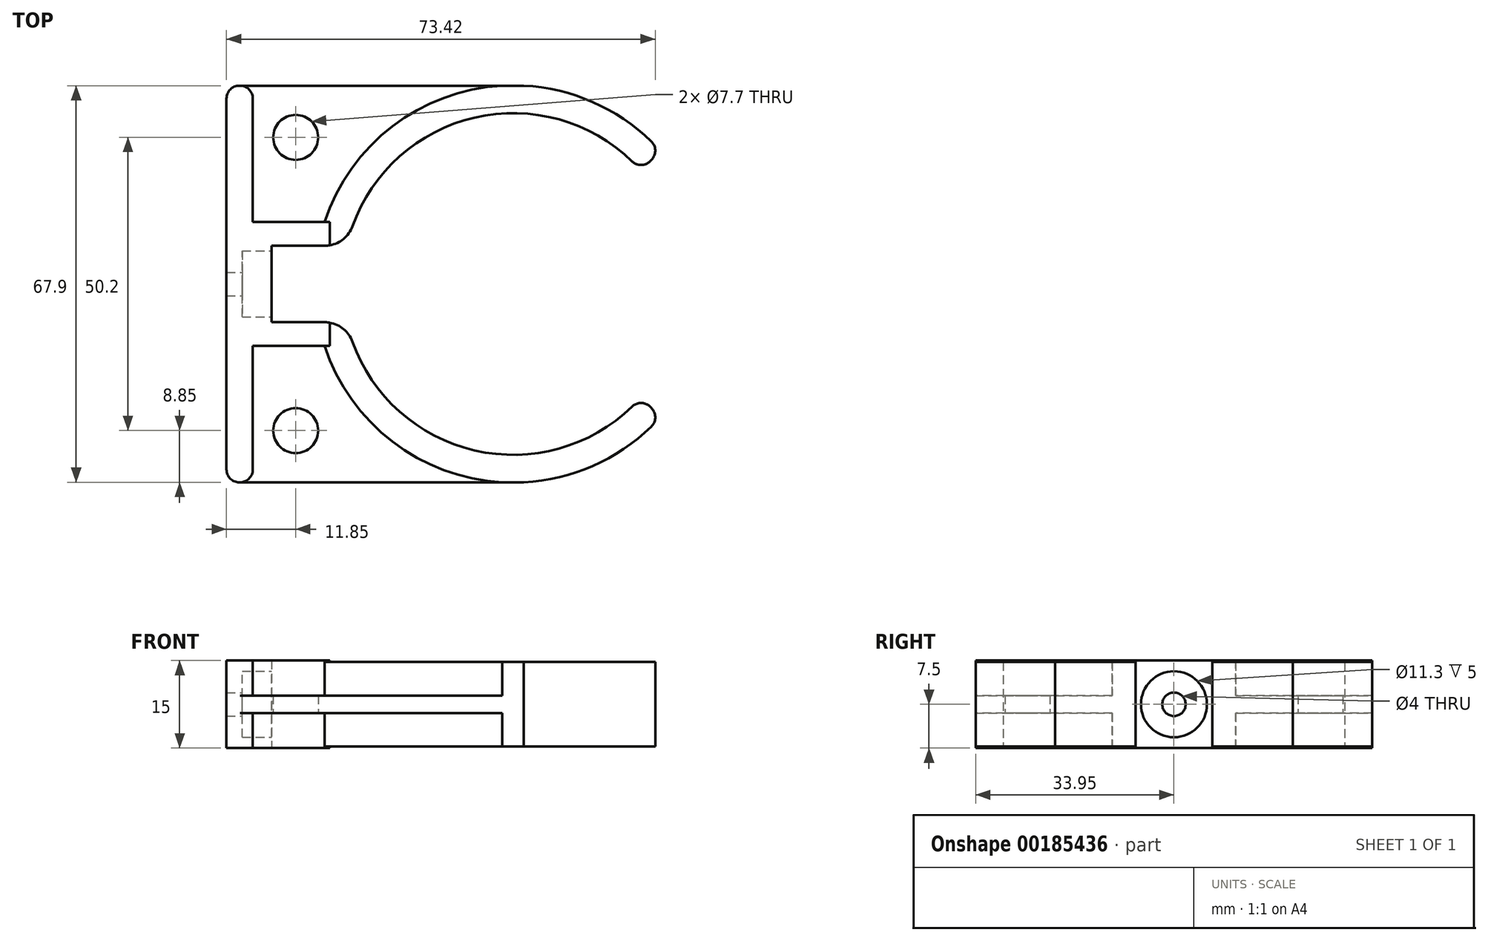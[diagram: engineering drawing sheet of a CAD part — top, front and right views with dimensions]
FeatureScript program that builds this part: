
annotation { "Feature Type Name" : "Feature", "Feature Type Description" : "" }
export const myFeature = defineFeature(function(context is Context, id is Id, definition is map)
    precondition{}
    {
        {
            var Q0;
            Q0=qCreatedBy(makeId("Top.planeOp"),FACE);
            var sketch = newSketch(context, id + "F0", { "sketchPlane" : qUnion([Q0])});
            skLineSegment(sketch, "E0.bottom", {"start": v(0.06, 33.95) * mm, "end": v(-0.06, 33.95) * mm});
            skLineSegment(sketch, "E0.top", {"start": v(0.06, -33.95) * mm, "end": v(-0.06, -33.95) * mm});
            skLineSegment(sketch, "E0.left", {"start": v(2.25, 31.76) * mm, "end": v(2.25, -31.76) * mm});
            skLineSegment(sketch, "E0.right", {"start": v(-2.25, 31.76) * mm, "end": v(-2.25, -31.76) * mm});
            skPoint(sketch, "E0.middle", {"position": v(0, 0) * mm});
            skPoint(sketch, "E1.visualSharp", {"position": v(-2.25, 33.95) * mm});
            skArc(sketch, "E1.filletArc", {"start": v(-0.06, 33.95) * mm, "mid": v(-1.6, 33.3) * mm, "end": v(-2.25, 31.76) * mm});
            skPoint(sketch, "E2.visualSharp", {"position": v(2.25, 33.95) * mm});
            skArc(sketch, "E2.filletArc", {"start": v(2.25, 31.76) * mm, "mid": v(1.6, 33.3) * mm, "end": v(0.06, 33.95) * mm});
            skPoint(sketch, "E3.visualSharp", {"position": v(-2.25, -33.95) * mm});
            skArc(sketch, "E3.filletArc", {"start": v(-2.25, -31.76) * mm, "mid": v(-1.6, -33.3) * mm, "end": v(-0.06, -33.95) * mm});
            skPoint(sketch, "E4.visualSharp", {"position": v(2.25, -33.95) * mm});
            skArc(sketch, "E4.filletArc", {"start": v(0.06, -33.95) * mm, "mid": v(1.6, -33.3) * mm, "end": v(2.25, -31.76) * mm});
            skSolve(sketch);
        }
        {
            var Q0;
            Q0 = qSketchRegion(id + "F0", true);
            extrude(context, id + "F1", {"entities" : qUnion([Q0]), "endBound" : BoundingType.SYMMETRIC, "depth" : 15 * mm});
        }
        {
            var Q0;
            Q0=qCreatedBy(makeId("Right.planeOp"),FACE);
            var sketch = newSketch(context, id + "F2", { "sketchPlane" : qUnion([Q0])});
            skLineSegment(sketch, "E5.left", {"start": v(10.6, 7.5) * mm, "end": v(10.6, -7.5) * mm});
            skLineSegment(sketch, "E5.right", {"start": v(-10.6, 7.5) * mm, "end": v(-10.6, -7.5) * mm});
            skPoint(sketch, "E5.middle", {"position": v(0, 0) * mm});
            skLineSegment(sketch, "E6.0.0", {"start": v(-10.6, -7.5) * mm, "end": v(10.6, -7.5) * mm});
            skLineSegment(sketch, "E6.0.2", {"start": v(10.6, 7.5) * mm, "end": v(-10.6, 7.5) * mm});
            skPoint(sketch, "E7.orphan", {"position": v(-10.6, 13.01) * mm});
            skPoint(sketch, "E8.orphan", {"position": v(10.6, 13.01) * mm});
            skPoint(sketch, "E5.top.start.orphan", {"position": v(10.6, -13.01) * mm});
            skPoint(sketch, "E9.orphan", {"position": v(-10.6, -13.01) * mm});
            skLineSegment(sketch, "E10", {"start": v(0, 7.5) * mm, "end": v(0, -7.5) * mm, "construction": true});
            skPoint(sketch, "E6.0.3.start.orphan", {"position": v(-31.76, 7.5) * mm});
            skPoint(sketch, "E11.orphan", {"position": v(-31.76, -7.5) * mm});
            skPoint(sketch, "E6.0.1.start.orphan", {"position": v(31.76, -7.5) * mm});
            skPoint(sketch, "E12.orphan", {"position": v(31.76, 7.5) * mm});
            skSolve(sketch);
        }
        {
            var Q0;
            Q0 = qSketchRegion(id + "F2", true);
            extrude(context, id + "F3", {"entities" : qUnion([Q0]), "operationType" : NewBodyOperationType.ADD, "depth" : 5.45 * mm});
        }
        {
            var Q0;
            Q0=makeQuery(id+"F3.opExtrude","CAP_FACE",FACE,{"disambiguationData":[OSD([sQuery(id+"F2.wireOp",EDGE,"E5.left"),sQuery(id+"F2.wireOp",EDGE,"E5.right"),sQuery(id+"F2.wireOp",EDGE,"E6.0.0"),sQuery(id+"F2.wireOp",EDGE,"E6.0.2")])],"isStart":false});
            var sketch = newSketch(context, id + "F4", { "sketchPlane" : qUnion([Q0])});
            skLineSegment(sketch, "E13.0.0", {"start": v(10.6, -7.5) * mm, "end": v(10.6, 7.5) * mm});
            skLineSegment(sketch, "E13.0.1", {"start": v(10.6, 7.5) * mm, "end": v(6.55, 7.5) * mm});
            skLineSegment(sketch, "E13.0.2", {"start": v(-10.6, 7.5) * mm, "end": v(-10.6, -7.5) * mm});
            skLineSegment(sketch, "E13.0.3", {"start": v(-10.6, -7.5) * mm, "end": v(-6.55, -7.5) * mm});
            skLineSegment(sketch, "E14.0", {"start": v(6.55, -7.5) * mm, "end": v(6.55, 7.5) * mm});
            skLineSegment(sketch, "E15.0", {"start": v(-6.55, 7.5) * mm, "end": v(-6.55, -7.5) * mm});
            skLineSegment(sketch, "E16.trimOffspring", {"start": v(-6.55, 7.5) * mm, "end": v(-10.6, 7.5) * mm});
            skLineSegment(sketch, "E17.trimOffspring", {"start": v(6.55, -7.5) * mm, "end": v(10.6, -7.5) * mm});
            skSolve(sketch);
        }
        {
            var Q0;
            Q0 = qSketchRegion(id + "F4", true);
            extrude(context, id + "F5", {"entities" : qUnion([Q0]), "operationType" : NewBodyOperationType.ADD, "depth" : 10 * mm});
        }
        {
            var Q0;
            Q0=qCreatedBy(makeId("Top.planeOp"),FACE);
            var sketch = newSketch(context, id + "F6", { "sketchPlane" : qUnion([Q0])});
            skLineSegment(sketch, "E18.0.0", {"start": v(2.25, -31.76) * mm, "end": v(2.25, -10.6) * mm});
            skLineSegment(sketch, "E18.0.1", {"start": v(2.25, -10.6) * mm, "end": v(15.45, -10.6) * mm});
            skLineSegment(sketch, "E18.0.2", {"start": v(15.45, -10.6) * mm, "end": v(15.45, -6.55) * mm});
            skLineSegment(sketch, "E18.0.3", {"start": v(15.45, -6.55) * mm, "end": v(5.45, -6.55) * mm});
            skLineSegment(sketch, "E18.0.4", {"start": v(5.45, -6.55) * mm, "end": v(5.45, 6.55) * mm});
            skLineSegment(sketch, "E18.0.5", {"start": v(5.45, 6.55) * mm, "end": v(15.45, 6.55) * mm});
            skLineSegment(sketch, "E18.0.6", {"start": v(15.45, 6.55) * mm, "end": v(15.45, 10.6) * mm});
            skLineSegment(sketch, "E18.0.7", {"start": v(15.45, 10.6) * mm, "end": v(2.25, 10.6) * mm});
            skLineSegment(sketch, "E18.0.8", {"start": v(2.25, 10.6) * mm, "end": v(2.25, 31.76) * mm});
            skArc(sketch, "E18.0.9", {"start": v(2.25, 31.76) * mm, "mid": v(1.6, 33.3) * mm, "end": v(0.06, 33.95) * mm});
            skLineSegment(sketch, "E18.0.10", {"start": v(0.06, 33.95) * mm, "end": v(-0.06, 33.95) * mm});
            skArc(sketch, "E18.0.11", {"start": v(-0.06, 33.95) * mm, "mid": v(-1.6, 33.3) * mm, "end": v(-2.25, 31.76) * mm});
            skLineSegment(sketch, "E18.0.12", {"start": v(-2.25, 31.76) * mm, "end": v(-2.25, -31.76) * mm});
            skArc(sketch, "E18.0.13", {"start": v(-2.25, -31.76) * mm, "mid": v(-1.6, -33.3) * mm, "end": v(-0.06, -33.95) * mm});
            skLineSegment(sketch, "E18.0.14", {"start": v(-0.06, -33.95) * mm, "end": v(0.06, -33.95) * mm});
            skArc(sketch, "E18.0.15", {"start": v(0.06, -33.95) * mm, "mid": v(1.6, -33.3) * mm, "end": v(2.25, -31.76) * mm});
            skLineSegment(sketch, "E19.bottom", {"start": v(0.06, -33.95) * mm, "end": v(48.68, -33.95) * mm});
            skLineSegment(sketch, "E19.left", {"start": v(0.06, -33.95) * mm, "end": v(0.06, 33.95) * mm});
            skLineSegment(sketch, "E19.right", {"start": v(68.85, -25.91) * mm, "end": v(68.85, -19.26) * mm});
            skLineSegment(sketch, "E20", {"start": v(0.06, 33.95) * mm, "end": v(48.68, 33.95) * mm});
            skPoint(sketch, "E21.first.point", {"position": v(19.45, 0) * mm});
            skPoint(sketch, "E21.second.point", {"position": v(72.85, 0) * mm});
            skArc(sketch, "E22", {"start": v(18.33, -6.55) * mm, "mid": v(38.56, -28.05) * mm, "end": v(67.22, -20.98) * mm});
            skArc(sketch, "E23", {"start": v(13.48, -6.55) * mm, "mid": v(36.68, -32.45) * mm, "end": v(70.5, -24.41) * mm});
            skLineSegment(sketch, "E24.trimOffspring", {"start": v(68.85, 19.26) * mm, "end": v(68.85, 25.91) * mm});
            skPoint(sketch, "E25.orphan", {"position": v(72.85, -33.95) * mm});
            skPoint(sketch, "E26.orphan", {"position": v(72.85, 33.95) * mm});
            skLineSegment(sketch, "E27", {"start": v(13.48, 6.55) * mm, "end": v(18.33, 6.55) * mm});
            skLineSegment(sketch, "E28", {"start": v(13.48, -6.55) * mm, "end": v(18.33, -6.55) * mm});
            skPoint(sketch, "E29.orphan", {"position": v(19.45, 6.55) * mm});
            skPoint(sketch, "E30.0.end.orphan", {"position": v(19.45, -6.55) * mm});
            skLineSegment(sketch, "E31", {"start": v(70.43, 21.15) * mm, "end": v(70.66, 21.43) * mm});
            skPoint(sketch, "E32.endSnap0", {"position": v(68.85, -22.59) * mm});
            skLineSegment(sketch, "E33", {"start": v(0, 0) * mm, "end": v(106.07, 0) * mm, "construction": true});
            skLineSegment(sketch, "E34.MirrorCS", {"start": v(70.43, -21.15) * mm, "end": v(70.66, -21.43) * mm});
            skArc(sketch, "E35.trimOffspring", {"start": v(70.5, 24.41) * mm, "mid": v(38.7, 33) * mm, "end": v(14.53, 10.6) * mm});
            skArc(sketch, "E36.trimOffspring", {"start": v(67.22, 20.98) * mm, "mid": v(38.56, 28.05) * mm, "end": v(18.33, 6.55) * mm});
            skPoint(sketch, "E37.visualSharp", {"position": v(68.85, 19.26) * mm});
            skArc(sketch, "E37.filletArc", {"start": v(67.22, 20.98) * mm, "mid": v(68.86, 20.37) * mm, "end": v(70.43, 21.15) * mm});
            skPoint(sketch, "E38.visualSharp", {"position": v(71.93, 22.95) * mm});
            skArc(sketch, "E38.filletArc", {"start": v(70.66, 21.43) * mm, "mid": v(71.17, 22.95) * mm, "end": v(70.5, 24.41) * mm});
            skPoint(sketch, "E39.visualSharp", {"position": v(68.85, -19.26) * mm});
            skArc(sketch, "E39.filletArc", {"start": v(70.43, -21.15) * mm, "mid": v(68.86, -20.37) * mm, "end": v(67.22, -20.98) * mm});
            skPoint(sketch, "E40.visualSharp", {"position": v(71.93, -22.95) * mm});
            skArc(sketch, "E40.filletArc", {"start": v(70.5, -24.41) * mm, "mid": v(71.17, -22.95) * mm, "end": v(70.66, -21.43) * mm});
            skLineSegment(sketch, "E41", {"start": v(9.6, -25.1) * mm, "end": v(9.6, 25.1) * mm, "construction": true});
            skCircle(sketch, "E42", {"center": v(9.6, 25.1) * mm, "radius": 3.85 * mm});
            skCircle(sketch, "E43", {"center": v(9.6, -25.1) * mm, "radius": 3.85 * mm});
            skSolve(sketch);
        }
        {
            var Q0;
            {var subQ1=sQuery(id+"F6.wireOp",EDGE,"E18.0.8");Q0=makeQuery(id+"F6.imprint","IMPRINT",FACE,{"disambiguationData":[TD([[makeQuery(id+"F6.imprint","IMPRINT",EDGE,{"derivedFrom":subQ1}),-1.0]])]});}
            var Q1;
            {var subQ5=sQuery(id+"F6.wireOp",EDGE,"E18.0.0");Q1=makeQuery(id+"F6.imprint","IMPRINT",FACE,{"disambiguationData":[TD([[makeQuery(id+"F6.imprint","IMPRINT",EDGE,{"derivedFrom":subQ5}),-1.0]])]});}
            extrude(context, id + "F7", {"entities" : qUnion([Q0, Q1]), "operationType" : NewBodyOperationType.ADD, "endBound" : BoundingType.SYMMETRIC, "depth" : 3 * mm});
        }
        {
            var Q0;
            {var subQ9=sQuery(id+"F6.wireOp",EDGE,"E18.0.6");Q0=makeQuery(id+"F6.imprint","IMPRINT",FACE,{"disambiguationData":[TD([[makeQuery(id+"F6.imprint","IMPRINT",EDGE,{"derivedFrom":subQ9}),-1.0]])]});}
            var Q1;
            {var subQ4=sQuery(id+"F6.wireOp",EDGE,"E18.0.2");Q1=makeQuery(id+"F6.imprint","IMPRINT",FACE,{"disambiguationData":[TD([[makeQuery(id+"F6.imprint","IMPRINT",EDGE,{"derivedFrom":subQ4}),-1.0]])]});}
            var Q2;
            {var subQ4=sQuery(id+"F6.wireOp",EDGE,"E31");Q2=makeQuery(id+"F6.imprint","IMPRINT",FACE,{"disambiguationData":[TD([[makeQuery(id+"F6.imprint","IMPRINT",EDGE,{"derivedFrom":subQ4}),1.0]])]});}
            var Q3;
            {var subQ1=sQuery(id+"F6.wireOp",EDGE,"E34.MirrorCS");Q3=makeQuery(id+"F6.imprint","IMPRINT",FACE,{"disambiguationData":[TD([[makeQuery(id+"F6.imprint","IMPRINT",EDGE,{"derivedFrom":subQ1}),-1.0]])]});}
            extrude(context, id + "F8", {"entities" : qUnion([Q0, Q1, Q2, Q3]), "operationType" : NewBodyOperationType.ADD, "endBound" : BoundingType.SYMMETRIC, "depth" : 14.5 * mm});
        }
        {
            var Q0;
            Q0=makeQuery(id+"F8.opExtrude","SWEPT_EDGE",EDGE,{"disambiguationData":[OSD([sQuery(id+"F6.wireOp",EDGE,"E27"),sQuery(id+"F6.wireOp",EDGE,"E36.trimOffspring")])]});
            var Q1;
            Q1=makeQuery(id+"F8.opExtrude","SWEPT_EDGE",EDGE,{"disambiguationData":[OSD([sQuery(id+"F6.wireOp",EDGE,"E22"),sQuery(id+"F6.wireOp",EDGE,"E28")])]});
            fillet(context, id + "F9", {"entities" : qUnion([Q0, Q1]), "radius" : 5 * mm, "tangentPropagation" : true, "allowEdgeOverflow" : false});
        }
        {
            var Q0;
            Q0=makeQuery(id+"F3.opExtrude","CAP_FACE",FACE,{"disambiguationData":[OSD([sQuery(id+"F2.wireOp",EDGE,"E5.left"),sQuery(id+"F2.wireOp",EDGE,"E5.right"),sQuery(id+"F2.wireOp",EDGE,"E6.0.0"),sQuery(id+"F2.wireOp",EDGE,"E6.0.2")])],"isStart":false});
            var sketch = newSketch(context, id + "F10", { "sketchPlane" : qUnion([Q0])});
            skCircle(sketch, "E44", {"center": v(0, 0) * mm, "radius": 5.65 * mm});
            skSolve(sketch);
        }
        {
            var Q0;
            Q0 = qSketchRegion(id + "F10", true);
            extrude(context, id + "F11", {"entities" : qUnion([Q0]), "operationType" : NewBodyOperationType.REMOVE, "oppositeDirection" : true, "depth" : 5 * mm});
        }
        {
            var Q0;
            Q0=makeQuery(id+"F11.boolean.opBoolean","COPY",FACE,{"derivedFrom":makeQuery(id+"F11.opExtrude","CAP_FACE",FACE,{"disambiguationData":[OSD([sQuery(id+"F10.wireOp",EDGE,"E44")])],"isStart":false})});
            var sketch = newSketch(context, id + "F12", { "sketchPlane" : qUnion([Q0])});
            skCircle(sketch, "E45", {"center": v(0, 0) * mm, "radius": 2 * mm});
            skSolve(sketch);
        }
        {
            var Q0;
            Q0 = qSketchRegion(id + "F12", true);
            extrude(context, id + "F13", {"entities" : qUnion([Q0]), "operationType" : NewBodyOperationType.REMOVE, "oppositeDirection" : true, "depth" : 25 * mm});
        }
    });
